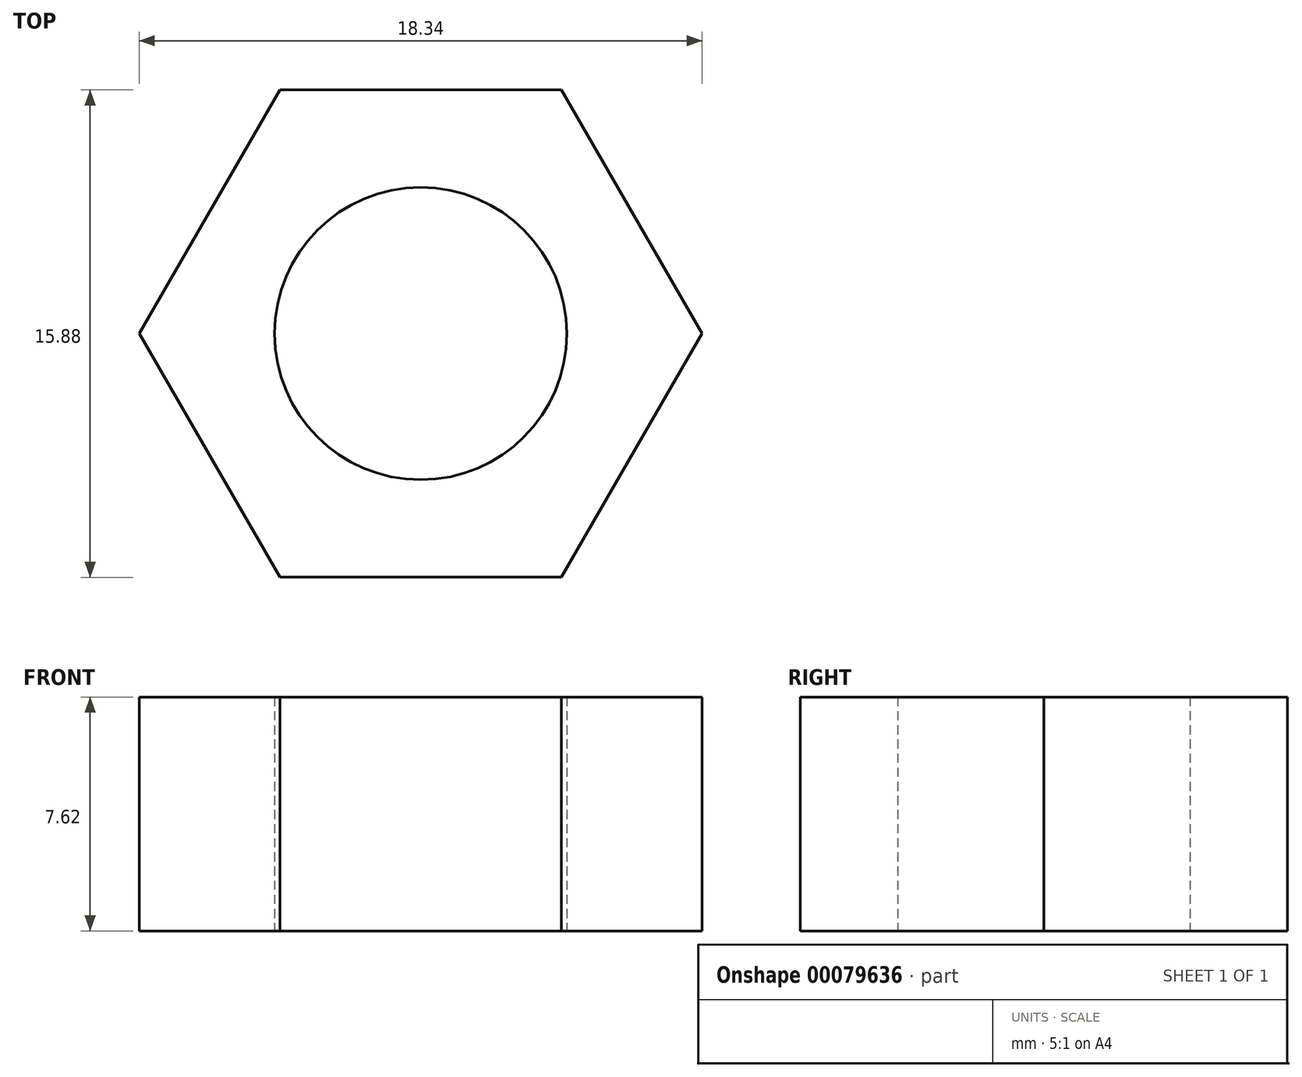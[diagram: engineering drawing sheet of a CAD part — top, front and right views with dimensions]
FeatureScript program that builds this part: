
annotation { "Feature Type Name" : "Feature", "Feature Type Description" : "" }
export const myFeature = defineFeature(function(context is Context, id is Id, definition is map)
    precondition{}
    {
        {
            var Q0;
            Q0=qCreatedBy(makeId("Top.planeOp"),FACE);
            var sketch = newSketch(context, id + "F0", { "sketchPlane" : qUnion([Q0])});
            skCircle(sketch, "E0.cCircle", {"center": v(0, 0) * mm, "radius": 7.94 * mm, "construction": true});
            skLineSegment(sketch, "E0.0", {"start": v(-4.58, 7.94) * mm, "end": v(4.58, 7.94) * mm});
            skLineSegment(sketch, "E0.1", {"start": v(4.58, 7.94) * mm, "end": v(9.17, 0) * mm});
            skLineSegment(sketch, "E0.2", {"start": v(9.17, 0) * mm, "end": v(4.58, -7.94) * mm});
            skLineSegment(sketch, "E0.3", {"start": v(4.58, -7.94) * mm, "end": v(-4.58, -7.94) * mm});
            skLineSegment(sketch, "E0.4", {"start": v(-4.58, -7.94) * mm, "end": v(-9.17, 0) * mm});
            skLineSegment(sketch, "E0.5", {"start": v(-9.17, 0) * mm, "end": v(-4.58, 7.94) * mm});
            skPoint(sketch, "E0.0.midPoint", {"position": v(0, 7.94) * mm});
            skSolve(sketch);
        }
        {
            var Q0;
            Q0=makeQuery(id+"F0.imprint","IMPRINT",FACE,{"disambiguationData":[TD([[makeQuery(id+"F0.imprint","IMPRINT",EDGE,{"derivedFrom":sQuery(id+"F0.wireOp",EDGE,"E0.0")}),-1.0]])]});
            extrude(context, id + "F1", {"entities" : qUnion([Q0]), "depth" : 7.62 * mm});
        }
        {
            var Q0;
            Q0=makeQuery(id+"F1.opExtrude","CAP_FACE",FACE,{"disambiguationData":[OSD([sQuery(id+"F0.wireOp",EDGE,"E0.0"),sQuery(id+"F0.wireOp",EDGE,"E0.1"),sQuery(id+"F0.wireOp",EDGE,"E0.2"),sQuery(id+"F0.wireOp",EDGE,"E0.3"),sQuery(id+"F0.wireOp",EDGE,"E0.4"),sQuery(id+"F0.wireOp",EDGE,"E0.5")])],"isStart":true});
            var sketch = newSketch(context, id + "F2", { "sketchPlane" : qUnion([Q0])});
            skCircle(sketch, "E1", {"center": v(0, 0) * mm, "radius": 4.76 * mm});
            skSolve(sketch);
        }
        {
            var Q0;
            Q0=makeQuery(id+"F2.imprint","IMPRINT",FACE,{"disambiguationData":[TD([[makeQuery(id+"F2.imprint","IMPRINT",EDGE,{"derivedFrom":sQuery(id+"F2.wireOp",EDGE,"E1")}),1.0]])]});
            extrude(context, id + "F3", {"entities" : qUnion([Q0]), "operationType" : NewBodyOperationType.REMOVE, "oppositeDirection" : true, "depth" : 25.4 * mm});
        }
    });
